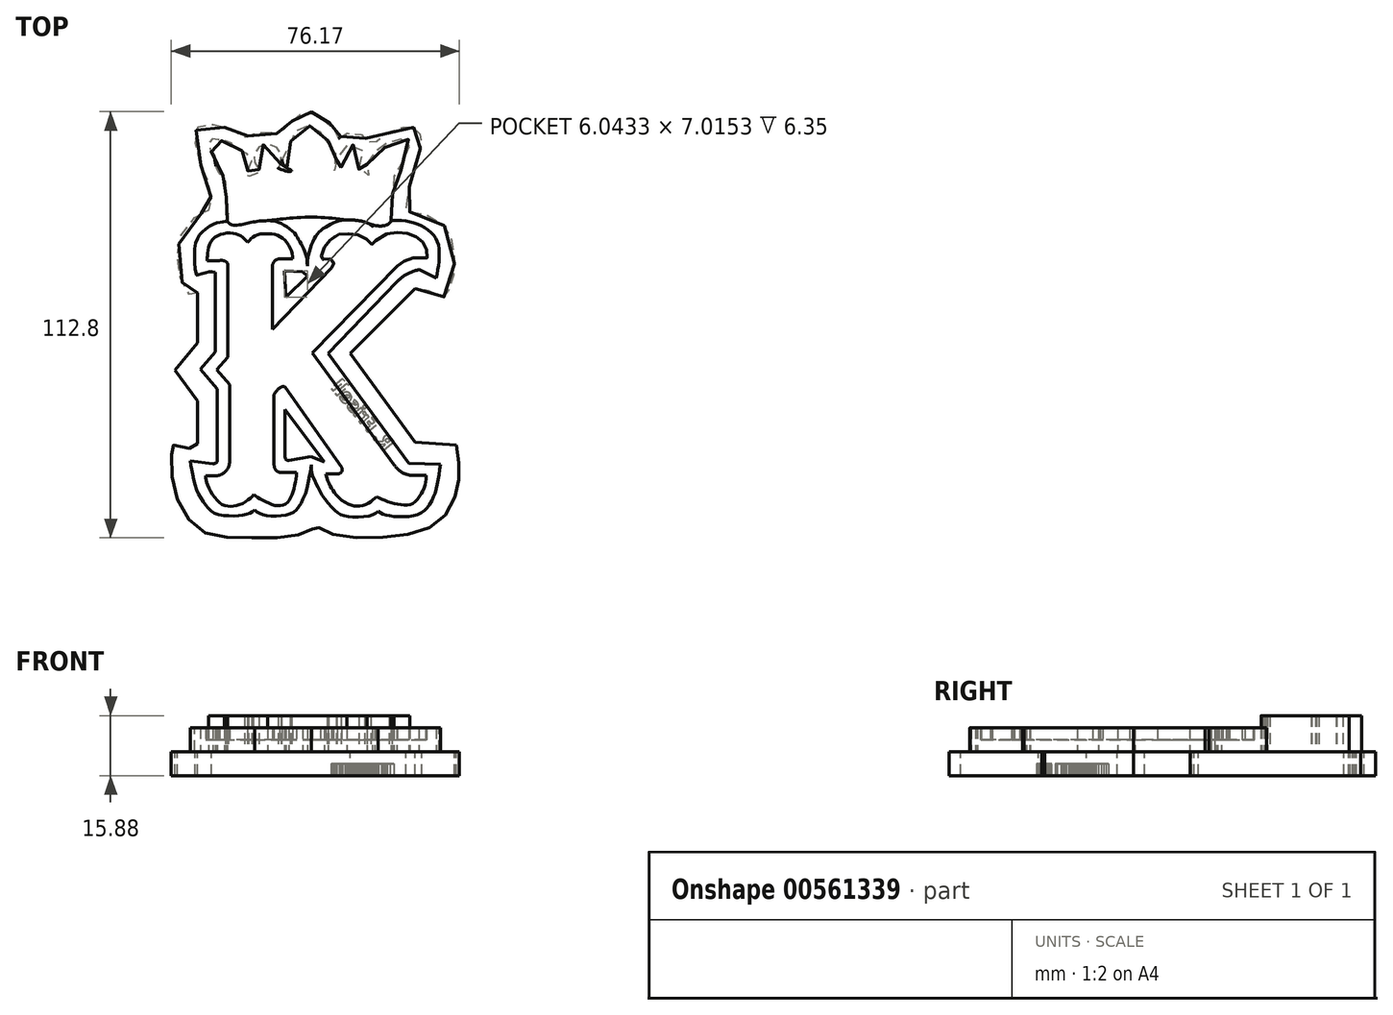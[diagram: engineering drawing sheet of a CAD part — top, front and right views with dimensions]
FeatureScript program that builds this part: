
annotation { "Feature Type Name" : "Feature", "Feature Type Description" : "" }
export const myFeature = defineFeature(function(context is Context, id is Id, definition is map)
    precondition{}
    {
        {
            var Q0;
            Q0=qCreatedBy(makeId("Top.planeOp"),FACE);
            var sketch = newSketch(context, id + "F0", { "sketchPlane" : qUnion([Q0])});
            skLineSegment(sketch, "E0", {"start": v(-21.56, -14.45) * mm, "end": v(-21.56, -33.71) * mm});
            skLineSegment(sketch, "E1", {"start": v(-28.7, -33.47) * mm, "end": v(-22.78, -34.26) * mm});
            skLineSegment(sketch, "E2", {"start": v(-2.66, -33.41) * mm, "end": v(3.13, -32.43) * mm});
            skLineSegment(sketch, "E3", {"start": v(-3.64, -20) * mm, "end": v(-3.64, -32.56) * mm});
            skLineSegment(sketch, "E4", {"start": v(-3.64, -20) * mm, "end": v(6.79, -33.84) * mm});
            skLineSegment(sketch, "E5", {"start": v(6.79, -33.84) * mm, "end": v(3.13, -32.43) * mm});
            skLineSegment(sketch, "E6", {"start": v(7.8, -5.09) * mm, "end": v(29.08, -34.13) * mm});
            skLineSegment(sketch, "E7", {"start": v(29.08, -34.13) * mm, "end": v(37.43, -34.43) * mm});
            skLineSegment(sketch, "E8", {"start": v(7.8, -5.09) * mm, "end": v(25.88, 13.8) * mm});
            skLineSegment(sketch, "E9", {"start": v(36.29, 14.84) * mm, "end": v(31.8, 17.14) * mm});
            skLineSegment(sketch, "E10", {"start": v(2.25, 15.4) * mm, "end": v(-3.4, 9.78) * mm});
            skLineSegment(sketch, "E11", {"start": v(-3.4, 9.78) * mm, "end": v(-3.8, 16.8) * mm});
            skLineSegment(sketch, "E12", {"start": v(-3.8, 16.8) * mm, "end": v(0.97, 16.48) * mm});
            skLineSegment(sketch, "E13", {"start": v(0.97, 16.48) * mm, "end": v(2.25, 15.4) * mm});
            skLineSegment(sketch, "E14", {"start": v(-21.56, -14.45) * mm, "end": v(-26, -9.3) * mm});
            skLineSegment(sketch, "E15", {"start": v(-26, -9.3) * mm, "end": v(-22.06, -4.7) * mm});
            skLineSegment(sketch, "E16", {"start": v(-22.06, -4.7) * mm, "end": v(-22.06, 16.37) * mm});
            skLineSegment(sketch, "E17", {"start": v(-18.75, 18.43) * mm, "end": v(-18.75, -6.12) * mm});
            skLineSegment(sketch, "E18", {"start": v(-18.75, -6.12) * mm, "end": v(-21.74, -9.35) * mm});
            skLineSegment(sketch, "E19", {"start": v(-21.74, -9.35) * mm, "end": v(-18.34, -13.28) * mm});
            skLineSegment(sketch, "E20", {"start": v(-18.34, -13.28) * mm, "end": v(-18.34, -33.83) * mm});
            skLineSegment(sketch, "E21", {"start": v(-6.62, -34.3) * mm, "end": v(-6.62, -16) * mm});
            skLineSegment(sketch, "E22", {"start": v(-3.53, -14.13) * mm, "end": v(11.3, -35.19) * mm});
            skLineSegment(sketch, "E23", {"start": v(-4.48, -36.63) * mm, "end": v(-0.58, -36.63) * mm});
            skLineSegment(sketch, "E24", {"start": v(7.12, -36.91) * mm, "end": v(10.18, -36.91) * mm});
            skLineSegment(sketch, "E25", {"start": v(-24.64, -37.42) * mm, "end": v(-21.52, -37.42) * mm});
            skLineSegment(sketch, "E26", {"start": v(33.61, -37.31) * mm, "end": v(29.28, -37.31) * mm});
            skLineSegment(sketch, "E27", {"start": v(25.14, -34.53) * mm, "end": v(3.59, -4.93) * mm});
            skLineSegment(sketch, "E28", {"start": v(3.59, -4.93) * mm, "end": v(26, 18.08) * mm});
            skLineSegment(sketch, "E29", {"start": v(8.6, 17.53) * mm, "end": v(-6.94, 1.21) * mm});
            skLineSegment(sketch, "E30", {"start": v(-6.94, 1.21) * mm, "end": v(-6.94, 18.4) * mm});
            skLineSegment(sketch, "E31", {"start": v(-1.6, 19.97) * mm, "end": v(-5.1, 19.97) * mm});
            skLineSegment(sketch, "E32", {"start": v(-24.32, 19.49) * mm, "end": v(-20.95, 19.49) * mm});
            skFitSpline(sketch, "E33", {"points": [v(-22.06, 16.37) * mm, v(-24.4, 16.37) * mm, v(-26.84, 15.6) * mm, v(-27.1, 15.72) * mm, v(-27.5, 23) * mm, v(-25.45, 27.1) * mm, v(-22.06, 29.3) * mm, v(-19.88, 29.77) * mm, v(-18.9, 29.8) * mm, v(-18.23, 29.12) * mm, v(-15.74, 28.91) * mm, v(-12.1, 29.67) * mm, v(-8.28, 30.04) * mm, v(-5.12, 29.49) * mm, v(-1.35, 26.9) * mm, v(0.2, 24.62) * mm, v(1.6, 21.82) * mm, v(2.26, 18.08) * mm, v(2.25, 15.4) * mm], "startDerivative": vector(-43.33, 5.47) * mm, "endDerivative": vector(-1.92, -46.92) * mm});
            skFitSpline(sketch, "E34", {"points": [v(2.26, 18.08) * mm, v(2.6, 21.3) * mm, v(4.36, 25.74) * mm, v(6.37, 27.86) * mm, v(9.54, 29.57) * mm, v(12.76, 30.25) * mm, v(17.7, 29.6) * mm, v(19.43, 28.54) * mm], "startDerivative": vector(0.74, 21.88) * mm, "endDerivative": vector(12.72, -10.42) * mm});
            skFitSpline(sketch, "E35", {"points": [v(19.43, 28.54) * mm, v(20.03, 28.8) * mm], "startDerivative": vector(0.6, 0.26) * mm, "endDerivative": vector(0.6, 0.26) * mm});
            skFitSpline(sketch, "E36", {"points": [v(-8.28, 30.04) * mm, v(-4.3, 30.5) * mm, v(4.1, 30.95) * mm, v(12.76, 30.25) * mm], "startDerivative": vector(14.05, 1.82) * mm, "endDerivative": vector(22.58, -2.67) * mm});
            skFitSpline(sketch, "E37", {"points": [v(17.7, 29.6) * mm, v(20.03, 28.8) * mm, v(22.96, 28.8) * mm, v(24.4, 30.04) * mm, v(24.2, 31.32) * mm, v(23.93, 32.4) * mm, v(24.66, 34.17) * mm, v(24.5, 36.42) * mm, v(25.08, 37.83) * mm, v(24.7, 39.46) * mm, v(25.08, 41.52) * mm, v(26.5, 42.68) * mm, v(27.3, 44.53) * mm, v(27.62, 46.86) * mm, v(28.88, 48.93) * mm, v(29.22, 51.15) * mm, v(28.01, 51.89) * mm, v(26.26, 51.4) * mm, v(24.5, 51.13) * mm, v(23.22, 50.55) * mm, v(22.47, 48.98) * mm, v(21.55, 48.6) * mm, v(19.72, 48.2) * mm, v(18.3, 46.81) * mm, v(18.07, 44.98) * mm, v(18.78, 43.88) * mm, v(18.88, 42.28) * mm, v(17.7, 42.02) * mm, v(16.03, 42.94) * mm, v(15.95, 43.85) * mm, v(17.18, 45.42) * mm, v(17.02, 48.3) * mm, v(15.43, 49.8) * mm, v(13.12, 50.16) * mm, v(10.48, 48.7) * mm, v(10.06, 46.7) * mm, v(11.21, 44.22) * mm, v(10.06, 43.46) * mm, v(7.89, 43.25) * mm, v(8.33, 43.62) * mm, v(9.85, 44.93) * mm, v(9.98, 46.55) * mm, v(9.83, 47.26) * mm, v(9.54, 48.64) * mm, v(7.84, 49.9) * mm, v(7.5, 50.47) * mm, v(7.81, 51.6) * mm, v(7.03, 53.25) * mm, v(5.38, 53.54) * mm, v(4.38, 54.4) * mm, v(3.31, 55.05) * mm, v(1.8, 55) * mm, v(0.2, 53.72) * mm, v(-1.43, 53.48) * mm, v(-2.29, 51.89) * mm, v(-2.19, 50.32) * mm, v(-4.02, 48.85) * mm, v(-4.54, 46.6) * mm, v(-3.68, 44.32) * mm, v(-2.1, 43.49) * mm, v(-1.92, 43.23) * mm, v(-2.55, 43.02) * mm, v(-5.5, 43.93) * mm, v(-5.43, 43.93) * mm, v(-4.88, 44.82) * mm, v(-4.7, 46.97) * mm, v(-5.01, 48.51) * mm, v(-6.92, 49.95) * mm, v(-9.56, 50.08) * mm, v(-11.6, 48.28) * mm, v(-11.97, 46.18) * mm, v(-10.9, 44.17) * mm, v(-10.59, 43.57) * mm, v(-11, 42.65) * mm, v(-12.13, 41.86) * mm, v(-14.3, 41.92) * mm, v(-13.65, 42.15) * mm, v(-13.41, 42.94) * mm, v(-13.6, 43.83) * mm, v(-12.94, 44.48) * mm, v(-12.44, 45.58) * mm, v(-13.44, 47.52) * mm, v(-15.09, 48.51) * mm, v(-16.26, 48.51) * mm, v(-17.28, 49.3) * mm, v(-17.86, 50.55) * mm, v(-19.56, 51.18) * mm, v(-20.71, 51.26) * mm, v(-21.97, 51.76) * mm, v(-22.94, 51.7) * mm, v(-23.72, 50.92) * mm, v(-23.64, 48.98) * mm, v(-22.7, 47.73) * mm, v(-22.2, 45.92) * mm, v(-21.7, 43.64) * mm, v(-20.97, 42.5) * mm, v(-20.03, 41.86) * mm, v(-19.4, 40.4) * mm, v(-19.5, 38.93) * mm, v(-19.74, 38.1) * mm, v(-19.54, 37.15) * mm, v(-19.2, 36.34) * mm, v(-19.4, 35.14) * mm, v(-19.27, 33.65) * mm, v(-18.7, 32.6) * mm, v(-18.83, 31.24) * mm, v(-18.9, 29.8) * mm], "startDerivative": vector(186.71, -75.66) * mm, "endDerivative": vector(0.08, -158.21) * mm});
            skFitSpline(sketch, "E38", {"points": [v(24.4, 30.04) * mm, v(27.22, 30.04) * mm, v(30.83, 29.3) * mm, v(33.93, 27.7) * mm, v(36.19, 25.4) * mm, v(37.04, 22.66) * mm, v(36.97, 18.67) * mm, v(36.29, 14.84) * mm], "startDerivative": vector(20.93, 0.93) * mm, "endDerivative": vector(-5.16, -24.6) * mm});
            skFitSpline(sketch, "E39", {"points": [v(25.88, 13.8) * mm, v(28.3, 15.73) * mm, v(31.8, 17.14) * mm], "startDerivative": vector(4.69, 4.42) * mm, "endDerivative": vector(7.09, 2.31) * mm});
            skFitSpline(sketch, "E40", {"points": [v(-28.7, -33.47) * mm, v(-28.2, -36.8) * mm, v(-27.06, -40.97) * mm, v(-25.53, -43.98) * mm, v(-23.91, -46.1) * mm, v(-21.73, -47.58) * mm, v(-17.82, -48.09) * mm, v(-14.7, -47.86) * mm, v(-12.71, -47.2) * mm, v(-11.75, -46.47) * mm], "startDerivative": vector(3.41, -26.72) * mm, "endDerivative": vector(11.88, 10.8) * mm});
            skFitSpline(sketch, "E41", {"points": [v(-11.75, -46.47) * mm, v(-10.25, -47.52) * mm, v(-6.95, -48.15) * mm, v(-2.56, -47.6) * mm, v(-0.3, -46.02) * mm, v(1.27, -43.3) * mm, v(1.95, -41.48) * mm, v(2.91, -37.11) * mm, v(3.31, -34.59) * mm, v(3.13, -32.43) * mm], "startDerivative": vector(14.81, -13.7) * mm, "endDerivative": vector(-3.12, 22.7) * mm});
            skFitSpline(sketch, "E42", {"points": [v(3.31, -34.59) * mm, v(3.62, -37.37) * mm, v(4.84, -40) * mm, v(6.34, -42.9) * mm, v(9.35, -46.47) * mm, v(11.33, -47.83) * mm, v(14.71, -48.4) * mm, v(19.43, -47.83) * mm, v(20.98, -46.9) * mm], "startDerivative": vector(0.62, -24.19) * mm, "endDerivative": vector(13.3, 11.03) * mm});
            skFitSpline(sketch, "E43", {"points": [v(20.98, -46.9) * mm, v(22.45, -47.66) * mm, v(25.5, -48.25) * mm, v(30.49, -48.02) * mm, v(33.43, -46.47) * mm, v(35.38, -43.58) * mm, v(36.63, -39.75) * mm, v(37.43, -34.43) * mm], "startDerivative": vector(14.13, -8.5) * mm, "endDerivative": vector(3.8, 31.77) * mm});
            skFitSpline(sketch, "E44", {"points": [v(-22.78, -34.26) * mm, v(-22.32, -34.23) * mm, v(-21.87, -34.08) * mm, v(-21.56, -33.71) * mm], "startDerivative": vector(1.4, 0.04) * mm, "endDerivative": vector(0.8, 1.22) * mm});
            skFitSpline(sketch, "E45", {"points": [v(-3.64, -32.56) * mm, v(-3.4, -33.21) * mm, v(-2.66, -33.41) * mm], "startDerivative": vector(0.27, -1.57) * mm, "endDerivative": vector(1.68, -0.15) * mm});
            skFitSpline(sketch, "E46", {"points": [v(-6.62, -16) * mm, v(-6.02, -15.15) * mm, v(-4.88, -14.1) * mm, v(-4.02, -13.81) * mm, v(-3.53, -14.13) * mm], "startDerivative": vector(2.02, 3.18) * mm, "endDerivative": vector(2.31, -2.21) * mm});
            skFitSpline(sketch, "E47", {"points": [v(-21.52, -37.42) * mm, v(-20.6, -37.21) * mm, v(-19.45, -36.34) * mm, v(-18.52, -34.96) * mm, v(-18.34, -33.83) * mm], "startDerivative": vector(4.24, 0.52) * mm, "endDerivative": vector(0.27, 4.7) * mm});
            skFitSpline(sketch, "E48", {"points": [v(-24.64, -37.42) * mm, v(-24.44, -38.85) * mm, v(-23.35, -41.47) * mm, v(-21.01, -44.58) * mm, v(-18.6, -45.52) * mm, v(-16.15, -45.28) * mm, v(-13.42, -43.85) * mm, v(-11.91, -42.46) * mm], "startDerivative": vector(0.96, -12.62) * mm, "endDerivative": vector(10.5, 10.83) * mm});
            skFitSpline(sketch, "E49", {"points": [v(-11.91, -42.46) * mm, v(-10.53, -43.37) * mm, v(-7.58, -44.88) * mm, v(-5.3, -45.41) * mm, v(-3.18, -44.7) * mm, v(-1.89, -42.6) * mm, v(-1, -39.68) * mm, v(-0.58, -36.63) * mm], "startDerivative": vector(10.56, -7.32) * mm, "endDerivative": vector(2.03, 19.54) * mm});
            skFitSpline(sketch, "E50", {"points": [v(-6.62, -34.3) * mm, v(-6.33, -35.53) * mm, v(-5.7, -36.33) * mm, v(-4.48, -36.63) * mm], "startDerivative": vector(0.6, -3.72) * mm, "endDerivative": vector(3.9, -0.49) * mm});
            skFitSpline(sketch, "E51", {"points": [v(11.3, -35.19) * mm, v(11.47, -35.99) * mm, v(10.95, -36.8) * mm, v(10.18, -36.91) * mm], "startDerivative": vector(0.94, -2.35) * mm, "endDerivative": vector(-2.54, 0.15) * mm});
            skFitSpline(sketch, "E52", {"points": [v(7.12, -36.91) * mm, v(8.01, -39.6) * mm, v(8.92, -41.15) * mm, v(10.37, -43) * mm, v(13.2, -45.04) * mm, v(15.33, -45.48) * mm, v(17.62, -45.1) * mm, v(19.45, -43.99) * mm, v(20.55, -43.04) * mm], "startDerivative": vector(6.06, -20.92) * mm, "endDerivative": vector(10.27, 9.27) * mm});
            skFitSpline(sketch, "E53", {"points": [v(20.55, -43.04) * mm, v(22.6, -43.93) * mm, v(25.26, -44.8) * mm, v(28.06, -45.23) * mm, v(30.19, -44.82) * mm, v(31.98, -42.83) * mm, v(33.19, -40.5) * mm, v(33.69, -38.28) * mm, v(33.61, -37.31) * mm], "startDerivative": vector(16.07, -7.23) * mm, "endDerivative": vector(-1.8, 10.57) * mm});
            skFitSpline(sketch, "E54", {"points": [v(29.28, -37.31) * mm, v(27.08, -36.5) * mm, v(25.14, -34.53) * mm], "startDerivative": vector(-4.77, 1.23) * mm, "endDerivative": vector(-3.52, 4.3) * mm});
            skFitSpline(sketch, "E55", {"points": [v(26, 18.08) * mm, v(27.61, 19.15) * mm, v(30.1, 20.2) * mm, v(32.56, 20.2) * mm, v(33.61, 19.9) * mm, v(33.9, 20.23) * mm, v(33.79, 22.2) * mm, v(33, 24.18) * mm, v(31.3, 25.55) * mm, v(29.28, 26.5) * mm, v(26.3, 26.86) * mm, v(23.3, 26.53) * mm, v(19.85, 24.21) * mm, v(19.47, 23.7) * mm, v(19.02, 24.17) * mm, v(17.47, 25.53) * mm, v(14.92, 26.38) * mm, v(12.23, 26.57) * mm, v(9.65, 26.03) * mm, v(7.32, 23.87) * mm, v(6.33, 22.03) * mm, v(5.83, 19.94) * mm, v(6, 19.73) * mm, v(7.12, 20.02) * mm, v(8.41, 19.9) * mm, v(9.16, 19.16) * mm, v(9.04, 17.94) * mm, v(8.6, 17.53) * mm], "startDerivative": vector(39.04, 27.41) * mm, "endDerivative": vector(-22.81, -13.94) * mm});
            skFitSpline(sketch, "E56", {"points": [v(-6.94, 18.4) * mm, v(-6.62, 19.1) * mm, v(-5.98, 19.7) * mm, v(-5.1, 19.97) * mm], "startDerivative": vector(0.82, 2.32) * mm, "endDerivative": vector(2.63, 0.58) * mm});
            skFitSpline(sketch, "E57", {"points": [v(-1.6, 19.97) * mm, v(-1.91, 21.93) * mm, v(-3.44, 24.54) * mm, v(-5.47, 26.08) * mm, v(-7.74, 26.55) * mm, v(-10.28, 26.47) * mm, v(-12.26, 25.59) * mm, v(-13.16, 24.7) * mm, v(-13.57, 24.33) * mm], "startDerivative": vector(-1, 15) * mm, "endDerivative": vector(-6.01, -4.7) * mm});
            skFitSpline(sketch, "E58", {"points": [v(-13.57, 24.33) * mm, v(-14.82, 25.59) * mm, v(-16.85, 26.62) * mm, v(-20.3, 26.5) * mm, v(-22.91, 24.88) * mm, v(-24.04, 22.08) * mm, v(-24.22, 19.97) * mm, v(-24.32, 19.49) * mm], "startDerivative": vector(-8.98, 10.08) * mm, "endDerivative": vector(-1.5, -5.84) * mm});
            skFitSpline(sketch, "E59", {"points": [v(-20.95, 19.49) * mm, v(-20.17, 19.49) * mm, v(-19.14, 19.08) * mm, v(-18.75, 18.43) * mm], "startDerivative": vector(2.3, 0.2) * mm, "endDerivative": vector(0.86, -2.26) * mm});
            skSolve(sketch);
        }
        {
            var Q0;
            Q0=makeQuery(id+"F0.imprint","IMPRINT",FACE,{"disambiguationData":[TD([[makeQuery(id+"F0.imprint","IMPRINT",EDGE,{"derivedFrom":sQuery(id+"F0.wireOp",EDGE,"E0")}),1.0]])]});
            extrude(context, id + "F1", {"entities" : qUnion([Q0]), "depth" : 6.35 * mm, "offsetDistance" : 25.4 * mm});
        }
        {
            var Q0;
            {var subQ0=sQuery(id+"F0.wireOp",EDGE,"E36");Q0=makeQuery(id+"F0.imprint","IMPRINT",FACE,{"disambiguationData":[TD([[makeQuery(id+"F0.imprint","IMPRINT",EDGE,{"derivedFrom":subQ0}),1.0]])]});}
            extrude(context, id + "F2", {"entities" : qUnion([Q0]), "operationType" : NewBodyOperationType.ADD, "depth" : 9.52 * mm, "offsetDistance" : 25.4 * mm});
        }
        {
            var Q0;
            Q0=makeQuery(id+"F0.imprint","IMPRINT",FACE,{"disambiguationData":[TD([[makeQuery(id+"F0.imprint","IMPRINT",EDGE,{"derivedFrom":sQuery(id+"F0.wireOp",EDGE,"E17")}),1.0]])]});
            extrude(context, id + "F3", {"entities" : qUnion([Q0]), "operationType" : NewBodyOperationType.ADD, "depth" : 3.17 * mm, "offsetDistance" : 25.4 * mm});
        }
        {
            var Q0;
            {var subQ0=sQuery(id+"F0.wireOp",EDGE,"E59");var subQ1=sQuery(id+"F0.wireOp",EDGE,"E58");var subQ2=sQuery(id+"F0.wireOp",EDGE,"E57");var subQ3=sQuery(id+"F0.wireOp",EDGE,"E56");var subQ4=sQuery(id+"F0.wireOp",EDGE,"E55");var subQ5=sQuery(id+"F0.wireOp",EDGE,"E54");var subQ6=sQuery(id+"F0.wireOp",EDGE,"E53");var subQ7=sQuery(id+"F0.wireOp",EDGE,"E52");var subQ8=sQuery(id+"F0.wireOp",EDGE,"E51");var subQ9=sQuery(id+"F0.wireOp",EDGE,"E50");var subQ10=sQuery(id+"F0.wireOp",EDGE,"E49");var subQ11=sQuery(id+"F0.wireOp",EDGE,"E48");var subQ12=sQuery(id+"F0.wireOp",EDGE,"E47");var subQ13=sQuery(id+"F0.wireOp",EDGE,"E46");var subQ14=sQuery(id+"F0.wireOp",EDGE,"E32");var subQ15=sQuery(id+"F0.wireOp",EDGE,"E31");var subQ16=sQuery(id+"F0.wireOp",EDGE,"E30");var subQ17=sQuery(id+"F0.wireOp",EDGE,"E29");var subQ18=sQuery(id+"F0.wireOp",EDGE,"E28");var subQ19=sQuery(id+"F0.wireOp",EDGE,"E27");var subQ20=sQuery(id+"F0.wireOp",EDGE,"E26");var subQ21=sQuery(id+"F0.wireOp",EDGE,"E25");var subQ22=sQuery(id+"F0.wireOp",EDGE,"E24");var subQ23=sQuery(id+"F0.wireOp",EDGE,"E23");var subQ24=sQuery(id+"F0.wireOp",EDGE,"E22");var subQ25=sQuery(id+"F0.wireOp",EDGE,"E21");var subQ26=sQuery(id+"F0.wireOp",EDGE,"E20");var subQ27=sQuery(id+"F0.wireOp",EDGE,"E19");var subQ28=sQuery(id+"F0.wireOp",EDGE,"E18");var subQ29=sQuery(id+"F0.wireOp",EDGE,"E17");var subQ30=sQuery(id+"F0.wireOp",EDGE,"E37");var subQ31=sQuery(id+"F0.wireOp",EDGE,"E34");var subQ32=sQuery(id+"F0.wireOp",EDGE,"E33");Q0=makeQuery(id+"F3.boolean.opBoolean","MERGE",FACE,{"derivedFrom":[makeQuery(id+"F2.boolean.opBoolean","MERGE",FACE,{"derivedFrom":[makeQuery(id+"F1.opExtrude","CAP_FACE",FACE,{"disambiguationData":[OSD([sQuery(id+"F0.wireOp",EDGE,"E0"),sQuery(id+"F0.wireOp",EDGE,"E1"),sQuery(id+"F0.wireOp",EDGE,"E2"),sQuery(id+"F0.wireOp",EDGE,"E3"),sQuery(id+"F0.wireOp",EDGE,"E4"),sQuery(id+"F0.wireOp",EDGE,"E5"),sQuery(id+"F0.wireOp",EDGE,"E6"),sQuery(id+"F0.wireOp",EDGE,"E7"),sQuery(id+"F0.wireOp",EDGE,"E8"),sQuery(id+"F0.wireOp",EDGE,"E9"),sQuery(id+"F0.wireOp",EDGE,"E10"),sQuery(id+"F0.wireOp",EDGE,"E11"),sQuery(id+"F0.wireOp",EDGE,"E12"),sQuery(id+"F0.wireOp",EDGE,"E13"),sQuery(id+"F0.wireOp",EDGE,"E14"),sQuery(id+"F0.wireOp",EDGE,"E15"),sQuery(id+"F0.wireOp",EDGE,"E16"),subQ29,subQ28,subQ27,subQ26,subQ25,subQ24,subQ23,subQ22,subQ21,subQ20,subQ19,subQ18,subQ17,subQ16,subQ15,subQ14,subQ32,subQ31,sQuery(id+"F0.wireOp",EDGE,"E35"),subQ30,sQuery(id+"F0.wireOp",EDGE,"E38"),sQuery(id+"F0.wireOp",EDGE,"E39"),sQuery(id+"F0.wireOp",EDGE,"E40"),sQuery(id+"F0.wireOp",EDGE,"E41"),sQuery(id+"F0.wireOp",EDGE,"E42"),sQuery(id+"F0.wireOp",EDGE,"E43"),sQuery(id+"F0.wireOp",EDGE,"E44"),sQuery(id+"F0.wireOp",EDGE,"E45"),subQ13,subQ12,subQ11,subQ10,subQ9,subQ8,subQ7,subQ6,subQ5,subQ4,subQ3,subQ2,subQ1,subQ0])],"isStart":true}),makeQuery(id+"F2.opExtrude","CAP_FACE",FACE,{"disambiguationData":[OSD([subQ32,subQ31,sQuery(id+"F0.wireOp",EDGE,"E36"),subQ30])],"isStart":true})]}),makeQuery(id+"F3.opExtrude","CAP_FACE",FACE,{"disambiguationData":[OSD([subQ29,subQ28,subQ27,subQ26,subQ25,subQ24,subQ23,subQ22,subQ21,subQ20,subQ19,subQ18,subQ17,subQ16,subQ15,subQ14,subQ13,subQ12,subQ11,subQ10,subQ9,subQ8,subQ7,subQ6,subQ5,subQ4,subQ3,subQ2,subQ1,subQ0])],"isStart":true})]});}
            var sketch = newSketch(context, id + "F4", { "sketchPlane" : qUnion([Q0])});
            skLineSegment(sketch, "E60", {"start": v(13.59, 5.07) * mm, "end": v(30.77, -12.04) * mm});
            skLineSegment(sketch, "E61", {"start": v(13.59, 5.07) * mm, "end": v(30.7, 28.6) * mm});
            skLineSegment(sketch, "E62", {"start": v(30.7, 28.6) * mm, "end": v(41.68, 29.4) * mm});
            skLineSegment(sketch, "E63", {"start": v(-26.75, 28.96) * mm, "end": v(-26.75, 17.6) * mm});
            skLineSegment(sketch, "E64", {"start": v(-26.75, 17.6) * mm, "end": v(-32.8, 9.5) * mm});
            skLineSegment(sketch, "E65", {"start": v(-32.8, 9.5) * mm, "end": v(-26.82, 2.27) * mm});
            skLineSegment(sketch, "E66", {"start": v(-26.82, 2.27) * mm, "end": v(-26.82, -10.86) * mm});
            skFitSpline(sketch, "E67", {"points": [v(-26.82, -10.86) * mm, v(-28.3, -10.27) * mm, v(-28.59, -10.2) * mm, v(-29.87, -11.58) * mm, v(-31.9, -17.4) * mm, v(-31.87, -22.86) * mm, v(-30.21, -28.24) * mm, v(-25.24, -32.27) * mm, v(-23.71, -32.96) * mm, v(-23.18, -33.3) * mm, v(-23.24, -35.68) * mm, v(-23.87, -40.15) * mm, v(-25.62, -44.03) * mm, v(-27.24, -49.81) * mm, v(-27.18, -53.9) * mm, v(-25.4, -55.69) * mm, v(-20.74, -55.06) * mm, v(-16.27, -53.4) * mm, v(-14.27, -52.16) * mm, v(-13.55, -52.34) * mm, v(-11.05, -53.31) * mm, v(-6.55, -53.5) * mm, v(-5.11, -52.84) * mm, v(-3.92, -54.31) * mm, v(-2.8, -55.94) * mm, v(-0.83, -56.81) * mm, v(0.23, -58.1) * mm, v(2.08, -58.88) * mm, v(4.14, -58.35) * mm, v(4.92, -57.16) * mm, v(6.99, -56.57) * mm, v(8.74, -55.03) * mm, v(9.8, -53.13) * mm, v(10.49, -51.75) * mm, v(11.16, -52.42) * mm, v(13.8, -53.23) * mm, v(17.18, -52.33) * mm, v(18.33, -50.87) * mm, v(20.07, -50.7) * mm, v(21.65, -52.33) * mm, v(26.72, -54.56) * mm, v(29.33, -54.9) * mm, v(31.08, -54.3) * mm, v(32.2, -52.42) * mm, v(32.48, -50.56) * mm, v(30.85, -45.8) * mm, v(29.24, -39.25) * mm, v(28.26, -33.6) * mm, v(28.51, -32.5) * mm, v(29.41, -32.35) * mm, v(34.9, -31.14) * mm, v(39.37, -27.43) * mm, v(40.92, -22.06) * mm, v(40.52, -13.67) * mm, v(38.64, -10.1) * mm, v(38.19, -9.81) * mm, v(34.87, -11.28) * mm, v(30.77, -12.04) * mm], "startDerivative": vector(-137.15, 52.96) * mm, "endDerivative": vector(-189.27, -15.06) * mm});
            skFitSpline(sketch, "E68", {"points": [v(41.68, 29.4) * mm, v(42.41, 35.62) * mm, v(41.68, 41.68) * mm, v(37.75, 48.93) * mm, v(29.15, 52.86) * mm, v(15.57, 53.83) * mm, v(6.23, 51.94) * mm, v(4.7, 50.87) * mm, v(3.41, 51.7) * mm, v(-1.85, 53.46) * mm, v(-14.15, 53.83) * mm, v(-24.96, 52.44) * mm, v(-31.52, 45.14) * mm, v(-33.74, 34.26) * mm, v(-33.32, 29.4) * mm, v(-33.05, 29.4) * mm, v(-27.5, 30.17) * mm, v(-26.75, 28.96) * mm], "startDerivative": vector(16.87, 106.55) * mm, "endDerivative": vector(0.06, -63.68) * mm});
            skSolve(sketch);
        }
        {
            var Q0;
            Q0 = qSketchRegion(id + "F4", true);
            extrude(context, id + "F5", {"entities" : qUnion([Q0]), "operationType" : NewBodyOperationType.ADD, "depth" : 6.35 * mm, "offsetDistance" : 25.4 * mm});
        }
        {
            var Q0;
            Q0=makeQuery(id+"F5.opExtrude","CAP_FACE",FACE,{"disambiguationData":[OSD([sQuery(id+"F4.wireOp",EDGE,"E60"),sQuery(id+"F4.wireOp",EDGE,"E61"),sQuery(id+"F4.wireOp",EDGE,"E62"),sQuery(id+"F4.wireOp",EDGE,"E63"),sQuery(id+"F4.wireOp",EDGE,"E64"),sQuery(id+"F4.wireOp",EDGE,"E65"),sQuery(id+"F4.wireOp",EDGE,"E66"),sQuery(id+"F4.wireOp",EDGE,"E67"),sQuery(id+"F4.wireOp",EDGE,"E68")])],"isStart":false});
            var sketch = newSketch(context, id + "F6", { "sketchPlane" : qUnion([Q0])});
            skText(sketch, "E69", { "text": "R. Frisell", "fontName": "OpenSans-Bold.ttf"});
            const initialGuessF6  = {"E69": [0.0226, 0.03114, -0.64279, -0.76604, 0.00381]};
            skSetInitialGuess(sketch, initialGuessF6);
            skSolve(sketch);
        }
        {
            var Q0;
            Q0 = qSketchRegion(id + "F6", true);
            extrude(context, id + "F7", {"entities" : qUnion([Q0]), "operationType" : NewBodyOperationType.REMOVE, "oppositeDirection" : true, "depth" : 3.17 * mm, "offsetDistance" : 25.4 * mm});
        }
    });
